# Revit family: CARE SUPPORT WELS 4 STAR ACCESSIBLE SHOWER GRAB RAIL 1000MM
name_source: partatom
category: Plumbing Fixtures
units: mm (PartAtom-declared; Revit-internal decimal feet)

## family parameters
Cut with Voids When Loaded = No
Host = Face
OmniClass Number = 23.45.05.14.17
OmniClass Title = Showers
Part Type = Normal
Room Calculation Point = No
Round Connector Dimension = Use Diameter
Shared = No

## types (1)
- CARE SUPPORT WELS 4 STAR ACCESSIBLE SHOWER GRAB RAIL 1000MM - CHROME
    Assembly Code = D2010710
    CW Connection = Yes
    Default Elevation = 0 mm  [stored 0 ft]
    Description = CARE SUPPORT WELS 4 STAR ACCESSIBLE SHOWER GRAB RAIL 1000MM - CHROME
    HW Connection = Yes
    Manufacturer = GWA Bathrooms & Kitchens
    Material = GWA_Metal-Chrome
    Material_Face = GWA-Plastic-White
    Material_Sprays = GWA-Plastic-General
    Model = 91129C4E
    URL = https://www.caroma.com.au
    Vent Connection = No
    Waste Connection = No

note: [stored X ft] marks values corroborated as IEEE doubles in the binary element streams (Revit-internal decimal feet)

## geometry (parser evidence)
native form markers: Blend x4, Sweep x3
no freeform markers — native parametric forms only
